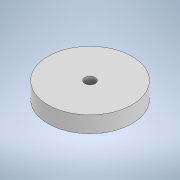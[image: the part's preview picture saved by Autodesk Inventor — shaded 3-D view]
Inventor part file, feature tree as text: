
AUTODESK INVENTOR PART (.ipt)
format: ipt  version: 2022 (Build 260153000, 153)  size: 95,232 bytes
history: native  units: mm
features: extrude x1, sketch x1
ambient origin geometry x8: Origin, YZ Plane, XZ Plane, XY Plane, X Axis, Y Axis, Z Axis, Center Point
bodies: Solid1 (feature_tree)
feature tree (2):
  extrude  "Extrusion1"  Depth=3.5mm
  sketch  "Sketch1"  dims[d0=18.0mm d1=2.25mm d2=3.5mm d3=0.0mm]
